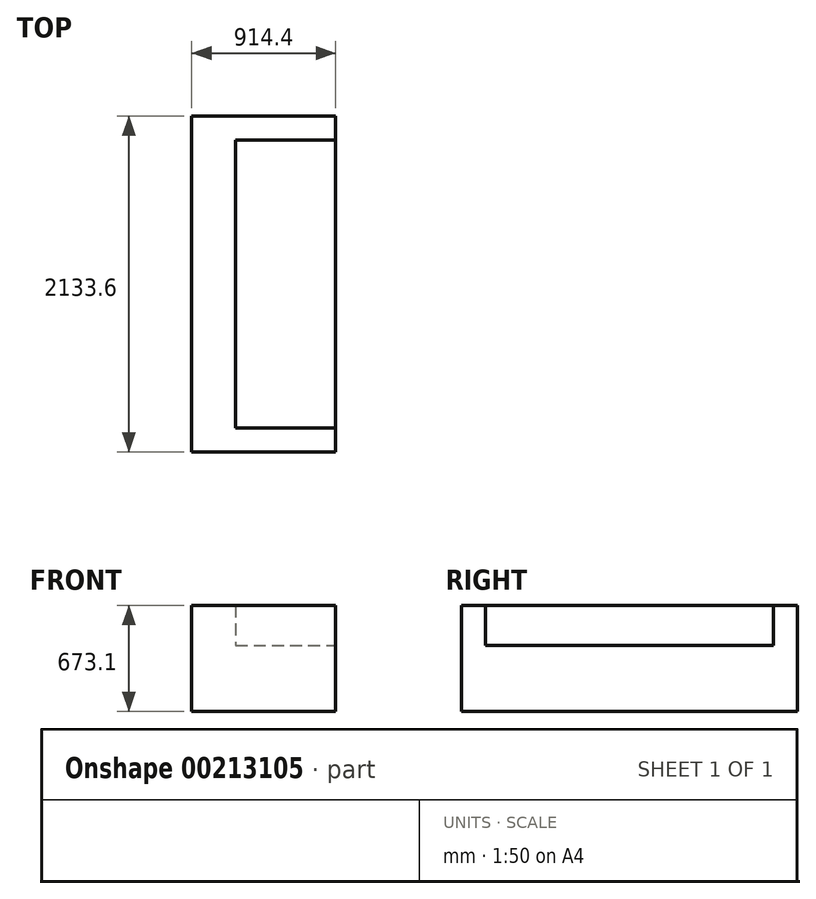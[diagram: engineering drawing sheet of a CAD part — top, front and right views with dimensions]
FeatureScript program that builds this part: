
annotation { "Feature Type Name" : "Feature", "Feature Type Description" : "" }
export const myFeature = defineFeature(function(context is Context, id is Id, definition is map)
    precondition{}
    {
        {
            var Q0;
            Q0=qCreatedBy(makeId("Front.planeOp"),FACE);
            var sketch = newSketch(context, id + "F0", { "sketchPlane" : qUnion([Q0])});
            skLineSegment(sketch, "E0.bottom", {"start": v(-28.14, 636.29) * mm, "end": v(886.26, 636.29) * mm});
            skLineSegment(sketch, "E0.top", {"start": v(-28.14, -36.81) * mm, "end": v(886.26, -36.81) * mm});
            skLineSegment(sketch, "E0.left", {"start": v(-28.14, 636.29) * mm, "end": v(-28.14, -36.81) * mm});
            skLineSegment(sketch, "E0.right", {"start": v(886.26, 636.29) * mm, "end": v(886.26, -36.81) * mm});
            skSolve(sketch);
        }
        {
            var Q0;
            Q0=makeQuery(id+"F0.imprint","IMPRINT",FACE,{"disambiguationData":[TD([[makeQuery(id+"F0.imprint","IMPRINT",EDGE,{"derivedFrom":sQuery(id+"F0.wireOp",EDGE,"E0.bottom")}),-1.0]])]});
            extrude(context, id + "F1", {"entities" : qUnion([Q0]), "depth" : 2133.6 * mm});
        }
        {
            var Q0;
            Q0=makeQuery(id+"F1.opExtrude","SWEPT_FACE",FACE,{"disambiguationData":[OSD([sQuery(id+"F0.wireOp",EDGE,"E0.right")])]});
            var sketch = newSketch(context, id + "F2", { "sketchPlane" : qUnion([Q0])});
            skLineSegment(sketch, "E1.bottom", {"start": v(-1981.2, 636.29) * mm, "end": v(-152.4, 636.29) * mm});
            skLineSegment(sketch, "E1.top", {"start": v(-1981.2, 382.29) * mm, "end": v(-152.4, 382.29) * mm});
            skLineSegment(sketch, "E1.left", {"start": v(-1981.2, 636.29) * mm, "end": v(-1981.2, 382.29) * mm});
            skLineSegment(sketch, "E1.right", {"start": v(-152.4, 636.29) * mm, "end": v(-152.4, 382.29) * mm});
            skSolve(sketch);
        }
        {
            var Q0;
            Q0=makeQuery(id+"F2.imprint","IMPRINT",FACE,{"disambiguationData":[TD([[makeQuery(id+"F2.imprint","IMPRINT",EDGE,{"derivedFrom":sQuery(id+"F2.wireOp",EDGE,"E1.bottom")}),-1.0]])]});
            extrude(context, id + "F3", {"entities" : qUnion([Q0]), "operationType" : NewBodyOperationType.REMOVE, "oppositeDirection" : true, "depth" : 635 * mm});
        }
    });
